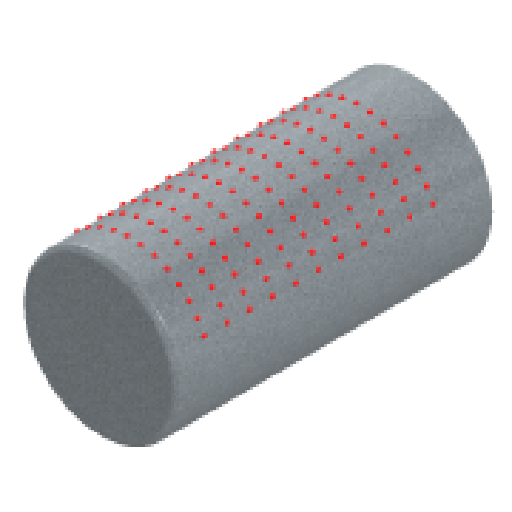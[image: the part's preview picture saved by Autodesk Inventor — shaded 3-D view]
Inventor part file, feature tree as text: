
AUTODESK INVENTOR PART (.ipt)
format: ipt  version: 2023 (Build 270158000, 158)  size: 564,224 bytes
history: native  units: in
note: dims shown in document units (in); Inventor stores cm internally (conversion verified against a paired STEP export)
features: extrude x3, sketch x3, fillet x2, chamfer x1, plane x1, pattern_linear x1, projected_geometry x1
ambient origin geometry x8: Origin, YZ Plane, XZ Plane, XY Plane, X Axis, Y Axis, Z Axis, Center Point
bodies: Solid1 (feature_tree)
feature tree (12):
  extrude  "Extrusion1"  Depth=137.7953in TaperAngle=0.0deg
  chamfer  "Chamfer1"  Distance=2.0in Angle=45.0deg
  fillet  "Fillet1"  Radius=2.0in
  plane  "Work Plane1"
  extrude  "Extrusion2"  Depth=4.7244in
  fillet  "Fillet2"  Radius=2.0in
  pattern_linear  "Rectangular Pattern1"  Spacing1=1.0in  [1 undecoded]
  extrude  "Extrusion3"  Depth=39.3701in
  sketch  "Sketch1"  dims[d0=78.7402in d1=137.7953in d2=0.0in d3=2.0in d4=0.125in d5=45.0deg d6=2.0in]
  sketch  "Sketch2"  dims[d7=-24.4375in d8=4.7244in d10=0.5497in d12=2.0in]
  sketch  "Sketch3"  dims[d13=2.0in d14=0.0in d15=1.0in d16=3.1496in d18=10.0in d19=39.3701in d20=0.0in]
  projected_geometry  "Projected Loop1"
note: 1 required parameter value undecoded (feature->parameter linkage not recoverable at this tier; creation-order binding heuristic only, values carry confidence <= 0.55)
